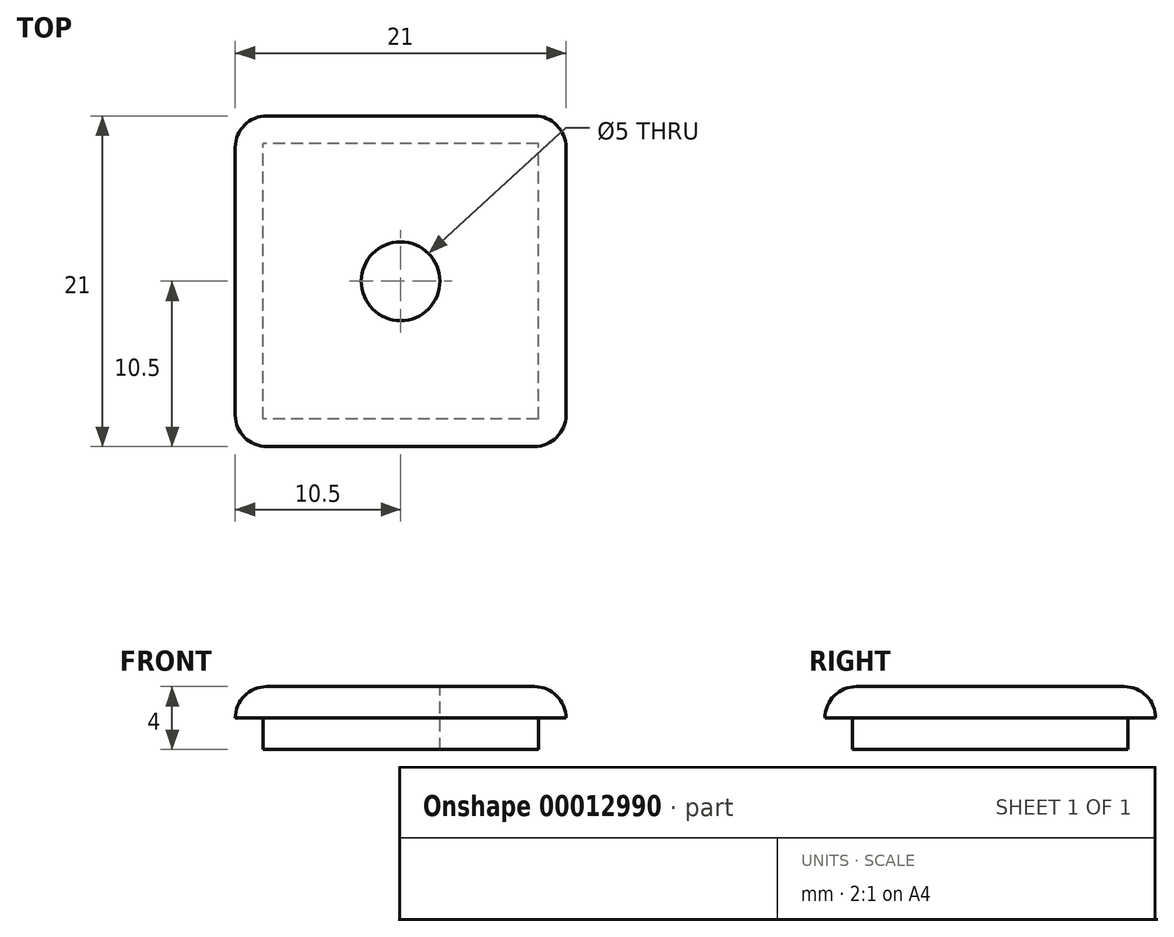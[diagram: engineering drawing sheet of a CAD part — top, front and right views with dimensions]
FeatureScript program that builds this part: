
annotation { "Feature Type Name" : "Feature", "Feature Type Description" : "" }
export const myFeature = defineFeature(function(context is Context, id is Id, definition is map)
    precondition{}
    {
        {
            var Q0;
            Q0=qCreatedBy(makeId("Top.planeOp"),FACE);
            var sketch = newSketch(context, id + "F0", { "sketchPlane" : qUnion([Q0])});
            skLineSegment(sketch, "E0.rect.bottom", {"start": v(8.5, -10.5) * mm, "end": v(-8.5, -10.5) * mm});
            skLineSegment(sketch, "E0.rect.top", {"start": v(8.5, 10.5) * mm, "end": v(-8.5, 10.5) * mm});
            skLineSegment(sketch, "E0.rect.left", {"start": v(10.5, -8.5) * mm, "end": v(10.5, 8.5) * mm});
            skLineSegment(sketch, "E0.rect.right", {"start": v(-10.5, -8.5) * mm, "end": v(-10.5, 8.5) * mm});
            skPoint(sketch, "E0.rect.middle", {"position": v(0, 0) * mm});
            skLineSegment(sketch, "E1.rect.bottom", {"start": v(8.75, -8.75) * mm, "end": v(-8.75, -8.75) * mm});
            skLineSegment(sketch, "E1.rect.top", {"start": v(8.75, 8.75) * mm, "end": v(-8.75, 8.75) * mm});
            skLineSegment(sketch, "E1.rect.left", {"start": v(8.75, -8.75) * mm, "end": v(8.75, 8.75) * mm});
            skLineSegment(sketch, "E1.rect.right", {"start": v(-8.75, -8.75) * mm, "end": v(-8.75, 8.75) * mm});
            skCircle(sketch, "E2", {"center": v(0, 0) * mm, "radius": 2.5 * mm});
            skPoint(sketch, "E3.visualSharp", {"position": v(-10.5, -10.5) * mm});
            skArc(sketch, "E3.filletArc", {"start": v(-10.5, -8.5) * mm, "mid": v(-9.91, -9.91) * mm, "end": v(-8.5, -10.5) * mm});
            skPoint(sketch, "E4.visualSharp", {"position": v(-10.5, 10.5) * mm});
            skArc(sketch, "E4.filletArc", {"start": v(-8.5, 10.5) * mm, "mid": v(-9.91, 9.91) * mm, "end": v(-10.5, 8.5) * mm});
            skPoint(sketch, "E5.visualSharp", {"position": v(10.5, 10.5) * mm});
            skArc(sketch, "E5.filletArc", {"start": v(10.5, 8.5) * mm, "mid": v(9.91, 9.91) * mm, "end": v(8.5, 10.5) * mm});
            skPoint(sketch, "E6.visualSharp", {"position": v(10.5, -10.5) * mm});
            skArc(sketch, "E6.filletArc", {"start": v(8.5, -10.5) * mm, "mid": v(9.91, -9.91) * mm, "end": v(10.5, -8.5) * mm});
            skSolve(sketch);
        }
        {
            var Q0;
            Q0=makeQuery(id+"F0.imprint","IMPRINT",FACE,{"disambiguationData":[TD([[makeQuery(id+"F0.imprint","IMPRINT",EDGE,{"derivedFrom":sQuery(id+"F0.wireOp",EDGE,"E1.rect.bottom")}),-1.0]])]});
            extrude(context, id + "F1", {"entities" : qUnion([Q0]), "oppositeDirection" : true, "depth" : 2 * mm});
        }
        {
            var Q0;
            Q0 = qSketchRegion(id + "F0", true);
            var Q1;
            Q1=makeQuery(id+"F1.opExtrude","CAP_FACE",FACE,{"disambiguationData":[OSD([sQuery(id+"F0.wireOp",EDGE,"E1.rect.bottom"),sQuery(id+"F0.wireOp",EDGE,"E1.rect.top"),sQuery(id+"F0.wireOp",EDGE,"E1.rect.left"),sQuery(id+"F0.wireOp",EDGE,"E1.rect.right"),sQuery(id+"F0.wireOp",EDGE,"E2")])],"isStart":true});
            extrude(context, id + "F2", {"entities" : qUnion([Q0, Q1]), "operationType" : NewBodyOperationType.ADD, "depth" : 2 * mm});
        }
        {
            var Q0;
            Q0=makeQuery(id+"F2.opExtrude","CAP_EDGE",EDGE,{"disambiguationData":[OSD([sQuery(id+"F0.wireOp",EDGE,"E0.rect.bottom")])],"isStart":false});
            var Q1;
            Q1=makeQuery(id+"F2.opExtrude","CAP_EDGE",EDGE,{"disambiguationData":[OSD([sQuery(id+"F0.wireOp",EDGE,"E0.rect.right")])],"isStart":false});
            var Q2;
            Q2=makeQuery(id+"F2.opExtrude","CAP_EDGE",EDGE,{"disambiguationData":[OSD([sQuery(id+"F0.wireOp",EDGE,"E0.rect.top")])],"isStart":false});
            var Q3;
            Q3=makeQuery(id+"F2.opExtrude","CAP_EDGE",EDGE,{"disambiguationData":[OSD([sQuery(id+"F0.wireOp",EDGE,"E0.rect.left")])],"isStart":false});
            fillet(context, id + "F3", {"entities" : qUnion([Q0, Q1, Q2, Q3]), "radius" : 2 * mm, "tangentPropagation" : true, "allowEdgeOverflow" : false});
        }
    });
